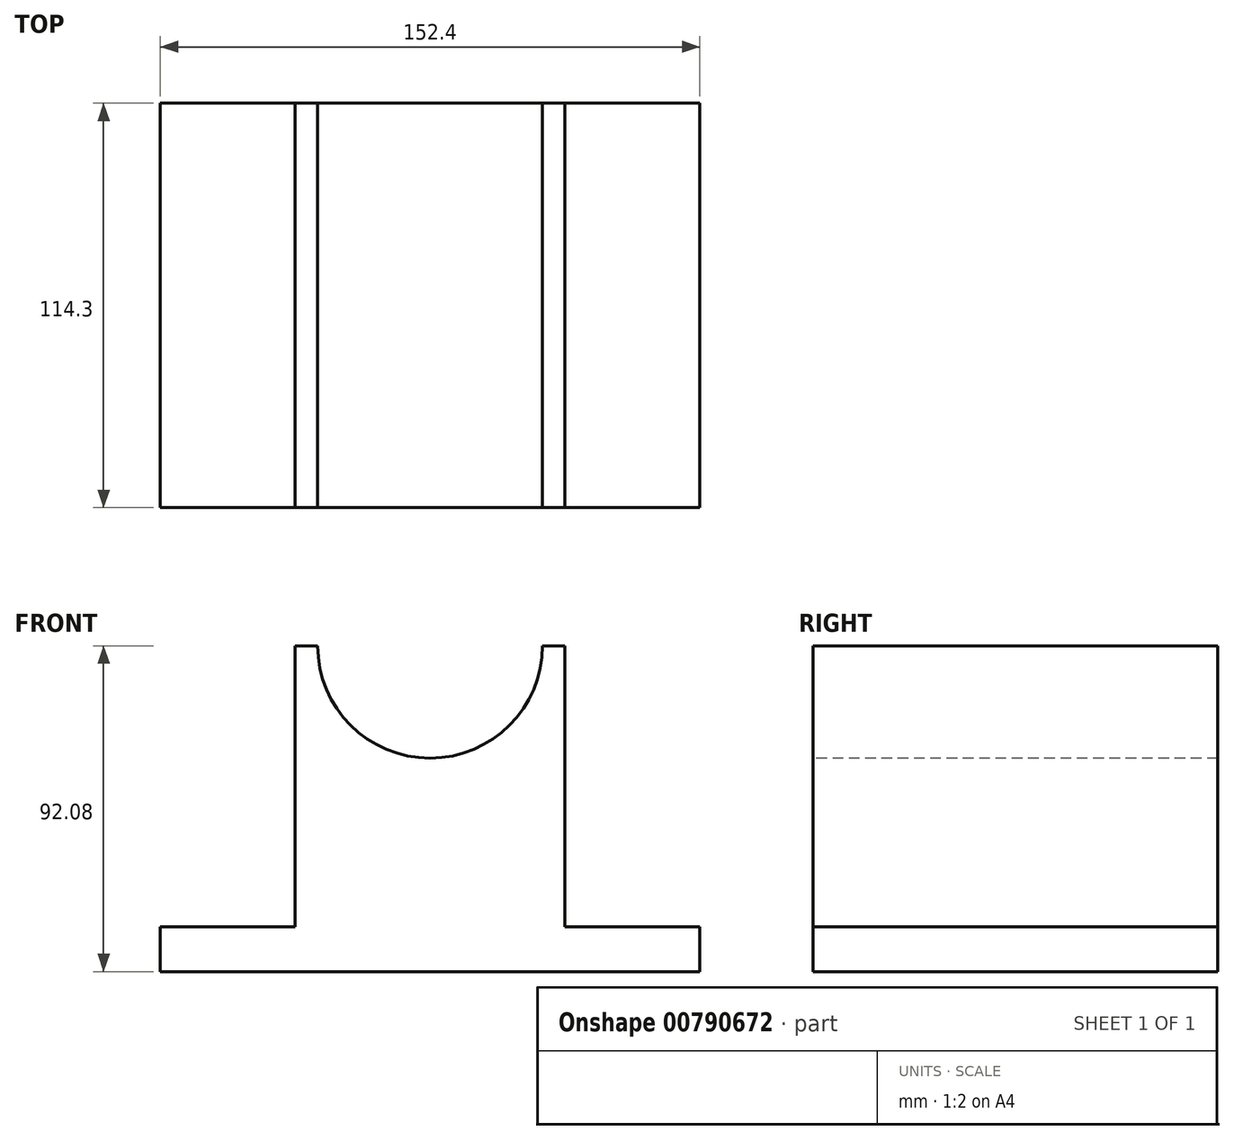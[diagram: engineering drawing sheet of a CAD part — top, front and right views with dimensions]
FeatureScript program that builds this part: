
annotation { "Feature Type Name" : "Feature", "Feature Type Description" : "" }
export const myFeature = defineFeature(function(context is Context, id is Id, definition is map)
    precondition{}
    {
        {
            var Q0;
            Q0=qCreatedBy(makeId("Front.planeOp"),FACE);
            var sketch = newSketch(context, id + "F0", { "sketchPlane" : qUnion([Q0])});
            skLineSegment(sketch, "E0", {"start": v(0, 0) * mm, "end": v(0, 12.7) * mm});
            skLineSegment(sketch, "E1", {"start": v(0, 12.7) * mm, "end": v(38.1, 12.7) * mm});
            skLineSegment(sketch, "E2", {"start": v(38.1, 12.7) * mm, "end": v(38.1, 92.08) * mm});
            skLineSegment(sketch, "E3", {"start": v(38.1, 92.08) * mm, "end": v(114.3, 92.08) * mm});
            skLineSegment(sketch, "E4", {"start": v(114.3, 92.08) * mm, "end": v(114.3, 12.7) * mm});
            skLineSegment(sketch, "E5", {"start": v(114.3, 12.7) * mm, "end": v(152.4, 12.7) * mm});
            skLineSegment(sketch, "E6", {"start": v(152.4, 12.7) * mm, "end": v(152.4, 0) * mm});
            skLineSegment(sketch, "E7", {"start": v(152.4, 0) * mm, "end": v(0, 0) * mm});
            skSolve(sketch);
        }
        {
            var Q0;
            Q0=makeQuery(id+"F0.imprint","IMPRINT",FACE,{"disambiguationData":[TD([[makeQuery(id+"F0.imprint","IMPRINT",EDGE,{"derivedFrom":sQuery(id+"F0.wireOp",EDGE,"E0")}),-1.0]])]});
            extrude(context, id + "F1", {"entities" : qUnion([Q0]), "depth" : 114.3 * mm, "offsetDistance" : 25.4 * mm});
        }
        {
            var Q0;
            Q0=makeQuery(id+"F1.opExtrude","CAP_FACE",FACE,{"disambiguationData":[OSD([sQuery(id+"F0.wireOp",EDGE,"E0"),sQuery(id+"F0.wireOp",EDGE,"E1"),sQuery(id+"F0.wireOp",EDGE,"E2"),sQuery(id+"F0.wireOp",EDGE,"E3"),sQuery(id+"F0.wireOp",EDGE,"E4"),sQuery(id+"F0.wireOp",EDGE,"E5"),sQuery(id+"F0.wireOp",EDGE,"E6"),sQuery(id+"F0.wireOp",EDGE,"E7")])],"isStart":false});
            var sketch = newSketch(context, id + "F2", { "sketchPlane" : qUnion([Q0])});
            skLineSegment(sketch, "E8", {"start": v(38.1, 92.08) * mm, "end": v(44.45, 92.08) * mm});
            skLineSegment(sketch, "E9", {"start": v(114.3, 92.08) * mm, "end": v(107.95, 92.08) * mm});
            skArc(sketch, "E10", {"start": v(44.45, 92.08) * mm, "mid": v(76.2, 60.33) * mm, "end": v(107.95, 92.08) * mm});
            skSolve(sketch);
        }
        {
            var Q0;
            {var subQ0=sQuery(id+"F2.wireOp",EDGE,"E10");Q0=makeQuery(id+"F2.imprint","IMPRINT",FACE,{"disambiguationData":[TD([[makeQuery(id+"F2.imprint","IMPRINT",EDGE,{"derivedFrom":subQ0}),1.0]])]});}
            extrude(context, id + "F3", {"entities" : qUnion([Q0]), "operationType" : NewBodyOperationType.REMOVE, "endBound" : BoundingType.THROUGH_ALL, "oppositeDirection" : true, "depth" : 25.4 * mm, "offsetDistance" : 25.4 * mm});
        }
    });
